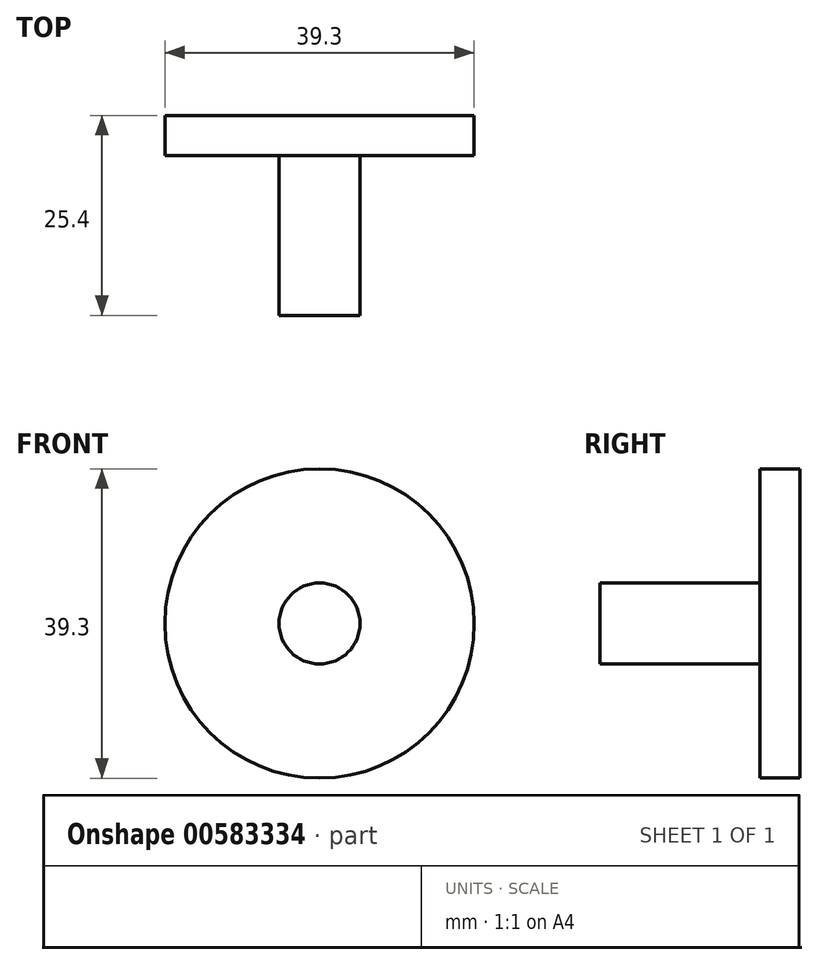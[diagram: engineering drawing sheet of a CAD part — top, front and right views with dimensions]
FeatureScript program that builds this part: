
annotation { "Feature Type Name" : "Feature", "Feature Type Description" : "" }
export const myFeature = defineFeature(function(context is Context, id is Id, definition is map)
    precondition{}
    {
        {
            var Q0;
            Q0=qCreatedBy(makeId("Front.planeOp"),FACE);
            var sketch = newSketch(context, id + "F0", { "sketchPlane" : qUnion([Q0])});
            skCircle(sketch, "E0", {"center": v(0, 0) * mm, "radius": 19.65 * mm});
            skCircle(sketch, "E1", {"center": v(0, 0) * mm, "radius": 5.08 * mm});
            skSolve(sketch);
        }
        {
            var Q0;
            Q0=makeQuery(id+"F0.imprint","IMPRINT",FACE,{"disambiguationData":[TD([[makeQuery(id+"F0.imprint","IMPRINT",EDGE,{"derivedFrom":sQuery(id+"F0.wireOp",EDGE,"E0")}),1.0]])]});
            extrude(context, id + "F1", {"entities" : qUnion([Q0]), "depth" : 5.08 * mm, "offsetDistance" : 25.4 * mm});
        }
        {
            var Q0;
            Q0=qCreatedBy(makeId("Front.planeOp"),FACE);
            var sketch = newSketch(context, id + "F2", { "sketchPlane" : qUnion([Q0])});
            skCircle(sketch, "E2", {"center": v(0, 0) * mm, "radius": 5.14 * mm});
            skSolve(sketch);
        }
        {
            var Q0;
            Q0 = qSketchRegion(id + "F2", true);
            extrude(context, id + "F3", {"entities" : qUnion([Q0]), "operationType" : NewBodyOperationType.ADD, "depth" : 25.4 * mm, "offsetDistance" : 25.4 * mm});
        }
    });
